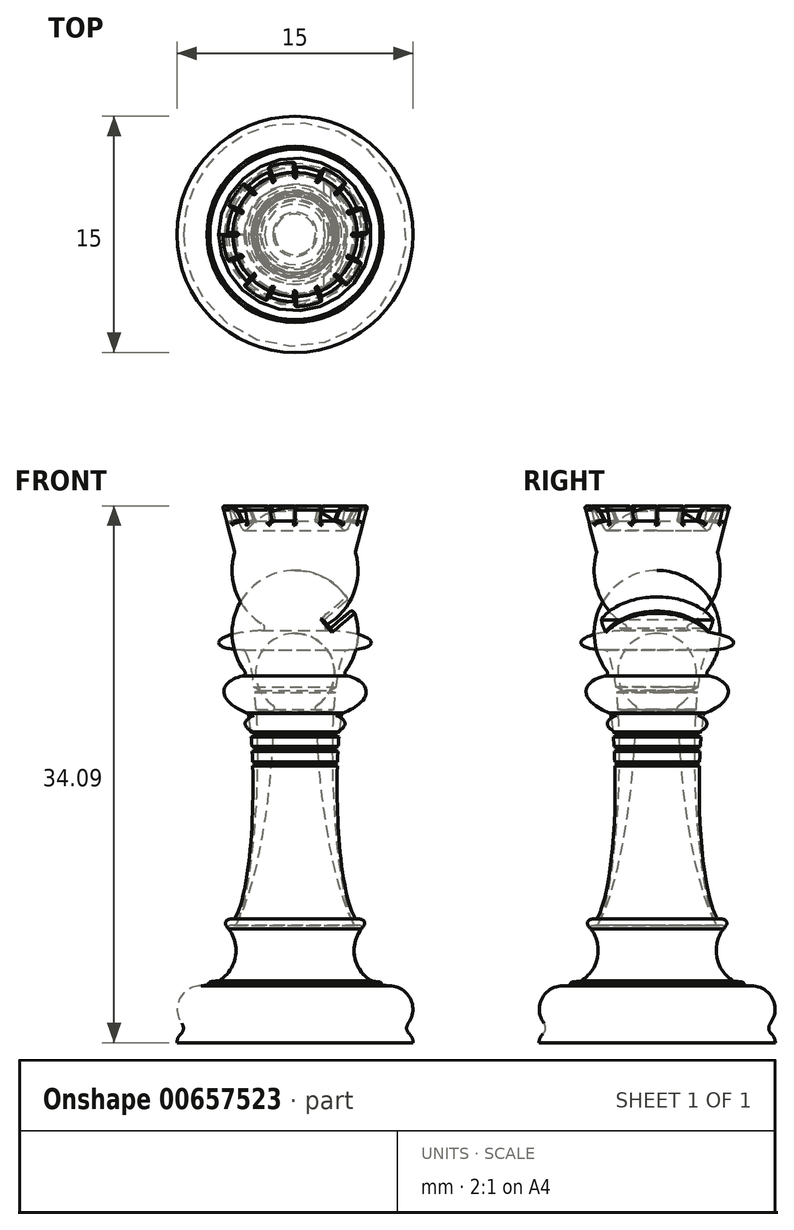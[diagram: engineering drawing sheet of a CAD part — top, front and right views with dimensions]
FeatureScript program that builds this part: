
annotation { "Feature Type Name" : "Feature", "Feature Type Description" : "" }
export const myFeature = defineFeature(function(context is Context, id is Id, definition is map)
    precondition{}
    {
        {
            var Q0;
            Q0=qCreatedBy(makeId("Front.planeOp"),FACE);
            var sketch = newSketch(context, id + "F0", { "sketchPlane" : qUnion([Q0])});
            skLineSegment(sketch, "E0", {"start": v(0, 0) * mm, "end": v(7.5, 0) * mm});
            skLineSegment(sketch, "E1", {"start": v(0, 0) * mm, "end": v(0, 26) * mm});
            skArc(sketch, "E2", {"start": v(7.5, 0) * mm, "mid": v(7.44, 0.3) * mm, "end": v(7.25, 0.56) * mm});
            skArc(sketch, "E3", {"start": v(7.19, 1.22) * mm, "mid": v(7.32, 2.8) * mm, "end": v(5.98, 3.62) * mm});
            skArc(sketch, "E4", {"start": v(1.39, 21.42) * mm, "mid": v(2.4, 24.23) * mm, "end": v(0, 26) * mm});
            skArc(sketch, "E5", {"start": v(4.23, 7.24) * mm, "mid": v(3.97, 4.88) * mm, "end": v(5.98, 3.62) * mm});
            skPoint(sketch, "E6.visualSharp", {"position": v(6.5, 0.7) * mm});
            skArc(sketch, "E6.filletArc", {"start": v(7.19, 1.22) * mm, "mid": v(7.1, 0.88) * mm, "end": v(7.25, 0.56) * mm});
            skFitSpline(sketch, "E7", {"points": [v(0.61, 21.08) * mm, v(3.13, 20.4) * mm, v(1.4, 19.5) * mm], "startDerivative": vector(4.88, 0.45) * mm, "endDerivative": vector(-7.93, 0.02) * mm});
            skFitSpline(sketch, "E8", {"points": [v(1.4, 19.5) * mm, v(3.8, 7.43) * mm], "startDerivative": vector(0.48, -12.4) * mm, "endDerivative": vector(4.03, -6.92) * mm});
            skFitSpline(sketch, "E9", {"points": [v(3.8, 7.43) * mm, v(4.23, 7.24) * mm], "startDerivative": vector(0.44, 0.11) * mm, "endDerivative": vector(-0.55, -0.65) * mm});
            skArc(sketch, "E10.filletArc", {"start": v(1.39, 21.42) * mm, "mid": v(1.3, 21.2) * mm, "end": v(1.48, 21.06) * mm});
            skArc(sketch, "E11.filletArc", {"start": v(1.6, 19.51) * mm, "mid": v(1.47, 19.45) * mm, "end": v(1.42, 19.3) * mm});
            skArc(sketch, "E12.filletArc", {"start": v(3.73, 7.55) * mm, "mid": v(3.8, 7.47) * mm, "end": v(3.91, 7.45) * mm});
            skSolve(sketch);
        }
        {
            var Q0;
            Q0=makeQuery(id+"F0.imprint","IMPRINT",FACE,{"disambiguationData":[TD([[makeQuery(id+"F0.imprint","IMPRINT",EDGE,{"derivedFrom":sQuery(id+"F0.wireOp",EDGE,"E0")}),1.0]])]});
            var Q1;
            Q1=sQuery(id+"F0.wireOp",EDGE,"E1");
            revolve(context, id + "F1", {"entities" : qUnion([Q0]), "axis" : qUnion([Q1]), "revolveType" : RevolveType.FULL});
        }
        {
            var Q0;
            Q0=qCreatedBy(makeId("Front.planeOp"),FACE);
            var sketch = newSketch(context, id + "F2", { "sketchPlane" : qUnion([Q0])});
            skLineSegment(sketch, "E13", {"start": v(0, 0) * mm, "end": v(7.5, 0) * mm});
            skLineSegment(sketch, "E14", {"start": v(0, 0) * mm, "end": v(0, 30) * mm});
            skArc(sketch, "E15", {"start": v(7.5, 0) * mm, "mid": v(7.44, 0.3) * mm, "end": v(7.25, 0.56) * mm});
            skArc(sketch, "E16", {"start": v(7.19, 1.22) * mm, "mid": v(7.32, 2.8) * mm, "end": v(5.98, 3.62) * mm});
            skArc(sketch, "E17", {"start": v(3.2, 23.6) * mm, "mid": v(3.58, 27.79) * mm, "end": v(0, 30) * mm});
            skArc(sketch, "E18", {"start": v(4.23, 7.24) * mm, "mid": v(3.97, 4.88) * mm, "end": v(5.98, 3.62) * mm});
            skPoint(sketch, "E19.visualSharp", {"position": v(6.5, 0.7) * mm});
            skArc(sketch, "E19.filletArc", {"start": v(7.19, 1.22) * mm, "mid": v(7.1, 0.88) * mm, "end": v(7.25, 0.56) * mm});
            skFitSpline(sketch, "E20", {"points": [v(2.96, 23.31) * mm, v(2.96, 20.9) * mm], "startDerivative": vector(4.36, -0.04) * mm, "endDerivative": vector(-7.84, -3.04) * mm});
            skFitSpline(sketch, "E21", {"points": [v(3.84, 7.87) * mm, v(2.96, 20.9) * mm], "startDerivative": vector(-3.7, 5.96) * mm, "endDerivative": vector(1.66, 9.57) * mm});
            skFitSpline(sketch, "E22", {"points": [v(4.23, 7.24) * mm, v(3.84, 7.87) * mm], "startDerivative": vector(1.52, 1.56) * mm, "endDerivative": vector(-0.97, -0.08) * mm});
            skArc(sketch, "E23.filletArc", {"start": v(3.2, 23.6) * mm, "mid": v(3.17, 23.4) * mm, "end": v(3.32, 23.28) * mm});
            skArc(sketch, "E24.filletArc", {"start": v(3.07, 20.94) * mm, "mid": v(2.98, 20.88) * mm, "end": v(2.94, 20.8) * mm});
            skArc(sketch, "E25.filletArc", {"start": v(3.78, 7.98) * mm, "mid": v(3.85, 7.9) * mm, "end": v(3.94, 7.87) * mm});
            skLineSegment(sketch, "E26", {"start": v(2.74, 18.81) * mm, "end": v(2.41, 18.65) * mm});
            skLineSegment(sketch, "E27", {"start": v(2.41, 18.65) * mm, "end": v(2.72, 18.5) * mm});
            skLineSegment(sketch, "E28", {"start": v(2.7, 17.84) * mm, "end": v(2.41, 17.71) * mm});
            skLineSegment(sketch, "E29", {"start": v(2.41, 17.71) * mm, "end": v(2.69, 17.58) * mm});
            skLineSegment(sketch, "E30", {"start": v(2.81, 19.75) * mm, "end": v(2.41, 19.55) * mm});
            skLineSegment(sketch, "E31", {"start": v(2.41, 19.55) * mm, "end": v(2.78, 19.41) * mm});
            skLineSegment(sketch, "E32", {"start": v(1.81, 26.84) * mm, "end": v(2.25, 26.32) * mm});
            skLineSegment(sketch, "E33", {"start": v(2.25, 26.32) * mm, "end": v(4.15, 27.94) * mm});
            skLineSegment(sketch, "E34", {"start": v(4.15, 27.94) * mm, "end": v(3.71, 28.45) * mm});
            skLineSegment(sketch, "E35", {"start": v(3.71, 28.45) * mm, "end": v(1.81, 26.84) * mm});
            skSolve(sketch);
        }
        {
            var Q0;
            Q0=makeQuery(id+"F2.imprint","IMPRINT",FACE,{"disambiguationData":[TD([[makeQuery(id+"F2.imprint","IMPRINT",EDGE,{"derivedFrom":sQuery(id+"F2.wireOp",EDGE,"E13")}),1.0]])]});
            var Q1;
            {var subQ5=sQuery(id+"F2.wireOp",EDGE,"E32");Q1=makeQuery(id+"F2.imprint","IMPRINT",FACE,{"disambiguationData":[TD([[makeQuery(id+"F2.imprint","IMPRINT",EDGE,{"derivedFrom":subQ5}),1.0]])]});}
            var Q2;
            Q2=sQuery(id+"F2.wireOp",EDGE,"E14");
            revolve(context, id + "F3", {"entities" : qUnion([Q0, Q1]), "axis" : qUnion([Q2]), "revolveType" : RevolveType.FULL});
        }
        {
            var Q0;
            {var subQ5=sQuery(id+"F2.wireOp",EDGE,"E34");Q0=makeQuery(id+"F2.imprint","IMPRINT",FACE,{"disambiguationData":[TD([[makeQuery(id+"F2.imprint","IMPRINT",EDGE,{"derivedFrom":subQ5}),1.0]])]});}
            var Q1;
            {var subQ5=sQuery(id+"F2.wireOp",EDGE,"E32");Q1=makeQuery(id+"F2.imprint","IMPRINT",FACE,{"disambiguationData":[TD([[makeQuery(id+"F2.imprint","IMPRINT",EDGE,{"derivedFrom":subQ5}),1.0]])]});}
            extrude(context, id + "F4", {"entities" : qUnion([Q0, Q1]), "operationType" : NewBodyOperationType.REMOVE, "endBound" : BoundingType.SYMMETRIC, "oppositeDirection" : true, "depth" : 25 * mm, "offsetDistance" : 25 * mm});
        }
        {
            var Q0;
            Q0=makeQuery(id+"F4.boolean.opBoolean","INTERSECT",EDGE,{"derivedFrom":[makeQuery(id+"F3.opRevolve","SWEPT_FACE",FACE,{"disambiguationData":[OSD([sQuery(id+"F2.wireOp",EDGE,"E17")])]}),makeQuery(id+"F4.opExtrude","SWEPT_FACE",FACE,{"disambiguationData":[OSD([sQuery(id+"F2.wireOp",EDGE,"E35")])]})]});
            var Q1;
            Q1=makeQuery(id+"F4.boolean.opBoolean","INTERSECT",EDGE,{"derivedFrom":[makeQuery(id+"F3.opRevolve","SWEPT_FACE",FACE,{"disambiguationData":[OSD([sQuery(id+"F2.wireOp",EDGE,"E17")])]}),makeQuery(id+"F4.opExtrude","SWEPT_FACE",FACE,{"disambiguationData":[OSD([sQuery(id+"F2.wireOp",EDGE,"E33")])]})]});
            var Q2;
            Q2=makeQuery(id+"F4.boolean.opBoolean","INTERSECT",EDGE,{"disambiguationData":[OD(0.0)],"derivedFrom":[makeQuery(id+"F3.opRevolve","SWEPT_FACE",FACE,{"disambiguationData":[OSD([sQuery(id+"F2.wireOp",EDGE,"E17")])]}),makeQuery(id+"F4.opExtrude","SWEPT_FACE",FACE,{"disambiguationData":[OSD([sQuery(id+"F2.wireOp",EDGE,"E32")])]})]});
            var Q3;
            Q3=makeQuery(id+"F4.boolean.opBoolean","INTERSECT",EDGE,{"disambiguationData":[OD(1.0)],"derivedFrom":[makeQuery(id+"F3.opRevolve","SWEPT_FACE",FACE,{"disambiguationData":[OSD([sQuery(id+"F2.wireOp",EDGE,"E17")])]}),makeQuery(id+"F4.opExtrude","SWEPT_FACE",FACE,{"disambiguationData":[OSD([sQuery(id+"F2.wireOp",EDGE,"E32")])]})]});
            fillet(context, id + "F5", {"entities" : qUnion([Q0, Q1, Q2, Q3]), "radius" : 0.2 * mm, "tangentPropagation" : true, "allowEdgeOverflow" : false});
        }
        {
            var Q0;
            Q0=qCreatedBy(makeId("Front.planeOp"),FACE);
            var sketch = newSketch(context, id + "F6", { "sketchPlane" : qUnion([Q0])});
            skLineSegment(sketch, "E36", {"start": v(0, 0) * mm, "end": v(7.5, 0) * mm});
            skLineSegment(sketch, "E37", {"start": v(0, 0) * mm, "end": v(0, 34) * mm});
            skArc(sketch, "E38", {"start": v(7.5, 0) * mm, "mid": v(7.44, 0.3) * mm, "end": v(7.25, 0.56) * mm});
            skArc(sketch, "E39", {"start": v(7.19, 1.22) * mm, "mid": v(7.32, 2.8) * mm, "end": v(5.98, 3.62) * mm});
            skArc(sketch, "E40", {"start": v(2.02, 26.55) * mm, "mid": v(3.71, 28.51) * mm, "end": v(3.85, 31.1) * mm});
            skArc(sketch, "E41", {"start": v(4.23, 7.24) * mm, "mid": v(3.78, 5.45) * mm, "end": v(4.84, 3.93) * mm});
            skPoint(sketch, "E42.visualSharp", {"position": v(6.5, 0.7) * mm});
            skArc(sketch, "E42.filletArc", {"start": v(7.19, 1.22) * mm, "mid": v(7.1, 0.88) * mm, "end": v(7.25, 0.56) * mm});
            skFitSpline(sketch, "E43", {"points": [v(1.23, 26.2) * mm, v(3.23, 24.96) * mm], "startDerivative": vector(12.28, 0.07) * mm, "endDerivative": vector(-7.93, 0.02) * mm});
            skFitSpline(sketch, "E44", {"points": [v(3.23, 24.96) * mm, v(3.8, 7.43) * mm], "startDerivative": vector(-4.36, -7.26) * mm, "endDerivative": vector(4.23, -6.86) * mm});
            skFitSpline(sketch, "E45", {"points": [v(3.8, 7.43) * mm, v(4.23, 7.24) * mm], "startDerivative": vector(0.44, 0.11) * mm, "endDerivative": vector(-0.55, -0.65) * mm});
            skArc(sketch, "E46.filletArc", {"start": v(2.02, 26.55) * mm, "mid": v(1.93, 26.33) * mm, "end": v(2.11, 26.18) * mm});
            skArc(sketch, "E47.filletArc", {"start": v(3.34, 24.96) * mm, "mid": v(3.24, 24.93) * mm, "end": v(3.17, 24.85) * mm});
            skArc(sketch, "E48.filletArc", {"start": v(3.73, 7.56) * mm, "mid": v(3.8, 7.48) * mm, "end": v(3.91, 7.45) * mm});
            skLineSegment(sketch, "E49", {"start": v(3.84, 31.2) * mm, "end": v(4.54, 33.84) * mm});
            skLineSegment(sketch, "E50", {"start": v(3.36, 32.65) * mm, "end": v(3.95, 33.78) * mm});
            skFitSpline(sketch, "E51", {"points": [v(3.95, 33.78) * mm, v(4.54, 33.84) * mm], "startDerivative": vector(0.92, 1.2) * mm, "endDerivative": vector(-0.55, -1.09) * mm});
            skLineSegment(sketch, "E52", {"start": v(3.61, 33.14) * mm, "end": v(4.3, 32.96) * mm});
            skArc(sketch, "E53.trimOffspring", {"start": v(3.03, 32.61) * mm, "mid": v(1.67, 33.64) * mm, "end": v(0, 34) * mm});
            skPoint(sketch, "E54.visualSharp", {"position": v(3.83, 31.15) * mm});
            skArc(sketch, "E54.filletArc", {"start": v(3.84, 31.2) * mm, "mid": v(3.84, 31.15) * mm, "end": v(3.85, 31.1) * mm});
            skPoint(sketch, "E55.visualSharp", {"position": v(3.22, 32.38) * mm});
            skArc(sketch, "E55.filletArc", {"start": v(3.03, 32.61) * mm, "mid": v(3.2, 32.54) * mm, "end": v(3.36, 32.65) * mm});
            skLineSegment(sketch, "E56", {"start": v(2.61, 22.58) * mm, "end": v(2.21, 22.37) * mm});
            skLineSegment(sketch, "E57", {"start": v(2.21, 22.37) * mm, "end": v(2.57, 22.24) * mm});
            skLineSegment(sketch, "E58", {"start": v(2.48, 21.18) * mm, "end": v(2.12, 21.04) * mm});
            skLineSegment(sketch, "E59", {"start": v(2.12, 21.04) * mm, "end": v(2.46, 20.88) * mm});
            skLineSegment(sketch, "E60", {"start": v(4.84, 3.93) * mm, "end": v(5.41, 3.87) * mm});
            skLineSegment(sketch, "E61", {"start": v(5.41, 3.87) * mm, "end": v(5.6, 3.65) * mm});
            skArc(sketch, "E62.trimOffspring", {"start": v(5.6, 3.65) * mm, "mid": v(5.8, 3.62) * mm, "end": v(5.98, 3.62) * mm});
            skSolve(sketch);
        }
        {
            var Q0;
            Q0=makeQuery(id+"F6.imprint","IMPRINT",FACE,{"disambiguationData":[TD([[makeQuery(id+"F6.imprint","IMPRINT",EDGE,{"derivedFrom":sQuery(id+"F6.wireOp",EDGE,"E36")}),1.0]])]});
            var Q1;
            Q1=sQuery(id+"F6.wireOp",EDGE,"E37");
            revolve(context, id + "F7", {"entities" : qUnion([Q0]), "axis" : qUnion([Q1]), "revolveType" : RevolveType.FULL});
        }
        {
            var Q0;
            {var subQ0=sQuery(id+"F6.wireOp",EDGE,"E51");Q0=makeQuery(id+"F6.imprint","IMPRINT",FACE,{"disambiguationData":[TD([[makeQuery(id+"F6.imprint","IMPRINT",EDGE,{"derivedFrom":subQ0}),-1.0]])]});}
            var Q1;
            Q1=sQuery(id+"F6.wireOp",EDGE,"E37");
            revolve(context, id + "F8", {"entities" : qUnion([Q0]), "axis" : qUnion([Q1]), "revolveType" : RevolveType.ONE_DIRECTION, "angle" : 22 * degree});
        }
        {
            var Q0;
            Q0=makeQuery(id+"F8.opRevolve","CAP_EDGE",EDGE,{"disambiguationData":[OSD([sQuery(id+"F6.wireOp",EDGE,"E50")])],"isStart":true});
            var Q1;
            Q1=makeQuery(id+"F8.opRevolve","CAP_EDGE",EDGE,{"disambiguationData":[OSD([sQuery(id+"F6.wireOp",EDGE,"E51")])],"isStart":true});
            var Q2;
            Q2=makeQuery(id+"F8.opRevolve","CAP_EDGE",EDGE,{"disambiguationData":[OSD([sQuery(id+"F6.wireOp",EDGE,"E49")])],"isStart":true});
            var Q3;
            Q3=makeQuery(id+"F8.opRevolve","CAP_EDGE",EDGE,{"disambiguationData":[OSD([sQuery(id+"F6.wireOp",EDGE,"E49")])],"isStart":false});
            var Q4;
            Q4=makeQuery(id+"F8.opRevolve","CAP_EDGE",EDGE,{"disambiguationData":[OSD([sQuery(id+"F6.wireOp",EDGE,"E51")])],"isStart":false});
            var Q5;
            Q5=makeQuery(id+"F8.opRevolve","CAP_EDGE",EDGE,{"disambiguationData":[OSD([sQuery(id+"F6.wireOp",EDGE,"E50")])],"isStart":false});
            fillet(context, id + "F9", {"entities" : qUnion([Q0, Q1, Q2, Q3, Q4, Q5]), "radius" : 0.1 * mm, "tangentPropagation" : true, "allowEdgeOverflow" : false});
        }
        {
            var Q0;
            Q0=makeQuery(id+"F8.opRevolve","SWEPT_BODY",BODY,{"disambiguationData":[OSD([sQuery(id+"F6.wireOp",EDGE,"E49"),sQuery(id+"F6.wireOp",EDGE,"E50"),sQuery(id+"F6.wireOp",EDGE,"E51"),sQuery(id+"F6.wireOp",EDGE,"E52")])]});
            var Q1;
            Q1=sQuery(id+"F6.wireOp",EDGE,"E37");
            circularPattern(context, id + "F10", {"operationType" : NewBodyOperationType.ADD, "entities" : qUnion([Q0]), "axis" : qUnion([Q1]), "angle" : 360 * degree, "instanceCount" : 8, "equalSpace" : true});
        }
        {
            var Q0;
            {var subQ3=sQuery(id+"F6.wireOp",EDGE,"E52");var subQ5=sQuery(id+"F6.wireOp",EDGE,"E49");Q0=makeQuery(id+"F10.boolean.opBoolean","SPLIT",FACE,{"disambiguationData":[TD([makeQuery(id+"F10.opPattern","COPY",FACE,{"derivedFrom":makeQuery(id+"F9.opFillet","BLEND_FACE",FACE,{"disambiguationData":[OSD([subQ5]),TDD([makeQuery(id+"F8.opRevolve","CAP_EDGE",EDGE,{"disambiguationData":[OSD([subQ5])],"isStart":false})])]}),"instanceName":"6"})])],"derivedFrom":makeQuery(id+"F7.opRevolve","SWEPT_FACE",FACE,{"disambiguationData":[OSD([subQ3])]})});}
            var Q1;
            {var subQ3=sQuery(id+"F6.wireOp",EDGE,"E49");var subQ6=sQuery(id+"F6.wireOp",EDGE,"E52");Q1=makeQuery(id+"F10.boolean.opBoolean","SPLIT",FACE,{"disambiguationData":[TD([makeQuery(id+"F9.opFillet","BLEND_FACE",FACE,{"disambiguationData":[OSD([subQ3]),TDD([makeQuery(id+"F8.opRevolve","CAP_EDGE",EDGE,{"disambiguationData":[OSD([subQ3])],"isStart":true})])]})])],"derivedFrom":makeQuery(id+"F7.opRevolve","SWEPT_FACE",FACE,{"disambiguationData":[OSD([subQ6])]})});}
            var Q2;
            {var subQ3=sQuery(id+"F6.wireOp",EDGE,"E49");var subQ6=sQuery(id+"F6.wireOp",EDGE,"E52");Q2=makeQuery(id+"F10.boolean.opBoolean","SPLIT",FACE,{"disambiguationData":[TD([makeQuery(id+"F9.opFillet","BLEND_FACE",FACE,{"disambiguationData":[OSD([subQ3]),TDD([makeQuery(id+"F8.opRevolve","CAP_EDGE",EDGE,{"disambiguationData":[OSD([subQ3])],"isStart":false})])]})])],"derivedFrom":makeQuery(id+"F7.opRevolve","SWEPT_FACE",FACE,{"disambiguationData":[OSD([subQ6])]})});}
            var Q3;
            {var subQ0=sQuery(id+"F6.wireOp",EDGE,"E49");var subQ6=sQuery(id+"F6.wireOp",EDGE,"E52");Q3=makeQuery(id+"F10.boolean.opBoolean","SPLIT",FACE,{"disambiguationData":[TD([makeQuery(id+"F10.opPattern","COPY",FACE,{"derivedFrom":makeQuery(id+"F9.opFillet","BLEND_FACE",FACE,{"disambiguationData":[OSD([subQ0]),TDD([makeQuery(id+"F8.opRevolve","CAP_EDGE",EDGE,{"disambiguationData":[OSD([subQ0])],"isStart":false})])]}),"instanceName":"1"})])],"derivedFrom":makeQuery(id+"F7.opRevolve","SWEPT_FACE",FACE,{"disambiguationData":[OSD([subQ6])]})});}
            var Q4;
            {var subQ3=sQuery(id+"F6.wireOp",EDGE,"E49");var subQ6=sQuery(id+"F6.wireOp",EDGE,"E52");Q4=makeQuery(id+"F10.boolean.opBoolean","SPLIT",FACE,{"disambiguationData":[TD([makeQuery(id+"F10.opPattern","COPY",FACE,{"derivedFrom":makeQuery(id+"F9.opFillet","BLEND_FACE",FACE,{"disambiguationData":[OSD([subQ3]),TDD([makeQuery(id+"F8.opRevolve","CAP_EDGE",EDGE,{"disambiguationData":[OSD([subQ3])],"isStart":false})])]}),"instanceName":"2"})])],"derivedFrom":makeQuery(id+"F7.opRevolve","SWEPT_FACE",FACE,{"disambiguationData":[OSD([subQ6])]})});}
            var Q5;
            {var subQ3=sQuery(id+"F6.wireOp",EDGE,"E49");var subQ6=sQuery(id+"F6.wireOp",EDGE,"E52");Q5=makeQuery(id+"F10.boolean.opBoolean","SPLIT",FACE,{"disambiguationData":[TD([makeQuery(id+"F10.opPattern","COPY",FACE,{"derivedFrom":makeQuery(id+"F9.opFillet","BLEND_FACE",FACE,{"disambiguationData":[OSD([subQ3]),TDD([makeQuery(id+"F8.opRevolve","CAP_EDGE",EDGE,{"disambiguationData":[OSD([subQ3])],"isStart":false})])]}),"instanceName":"3"})])],"derivedFrom":makeQuery(id+"F7.opRevolve","SWEPT_FACE",FACE,{"disambiguationData":[OSD([subQ6])]})});}
            var Q6;
            {var subQ0=sQuery(id+"F6.wireOp",EDGE,"E49");var subQ6=sQuery(id+"F6.wireOp",EDGE,"E52");Q6=makeQuery(id+"F10.boolean.opBoolean","SPLIT",FACE,{"disambiguationData":[TD([makeQuery(id+"F10.opPattern","COPY",FACE,{"derivedFrom":makeQuery(id+"F9.opFillet","BLEND_FACE",FACE,{"disambiguationData":[OSD([subQ0]),TDD([makeQuery(id+"F8.opRevolve","CAP_EDGE",EDGE,{"disambiguationData":[OSD([subQ0])],"isStart":false})])]}),"instanceName":"4"})])],"derivedFrom":makeQuery(id+"F7.opRevolve","SWEPT_FACE",FACE,{"disambiguationData":[OSD([subQ6])]})});}
            var Q7;
            {var subQ3=sQuery(id+"F6.wireOp",EDGE,"E49");var subQ6=sQuery(id+"F6.wireOp",EDGE,"E52");Q7=makeQuery(id+"F10.boolean.opBoolean","SPLIT",FACE,{"disambiguationData":[TD([makeQuery(id+"F10.opPattern","COPY",FACE,{"derivedFrom":makeQuery(id+"F9.opFillet","BLEND_FACE",FACE,{"disambiguationData":[OSD([subQ3]),TDD([makeQuery(id+"F8.opRevolve","CAP_EDGE",EDGE,{"disambiguationData":[OSD([subQ3])],"isStart":false})])]}),"instanceName":"5"})])],"derivedFrom":makeQuery(id+"F7.opRevolve","SWEPT_FACE",FACE,{"disambiguationData":[OSD([subQ6])]})});}
            fillet(context, id + "F11", {"entities" : qUnion([Q0, Q1, Q2, Q3, Q4, Q5, Q6, Q7]), "radius" : 0.1 * mm, "tangentPropagation" : true, "allowEdgeOverflow" : false});
        }
    });
